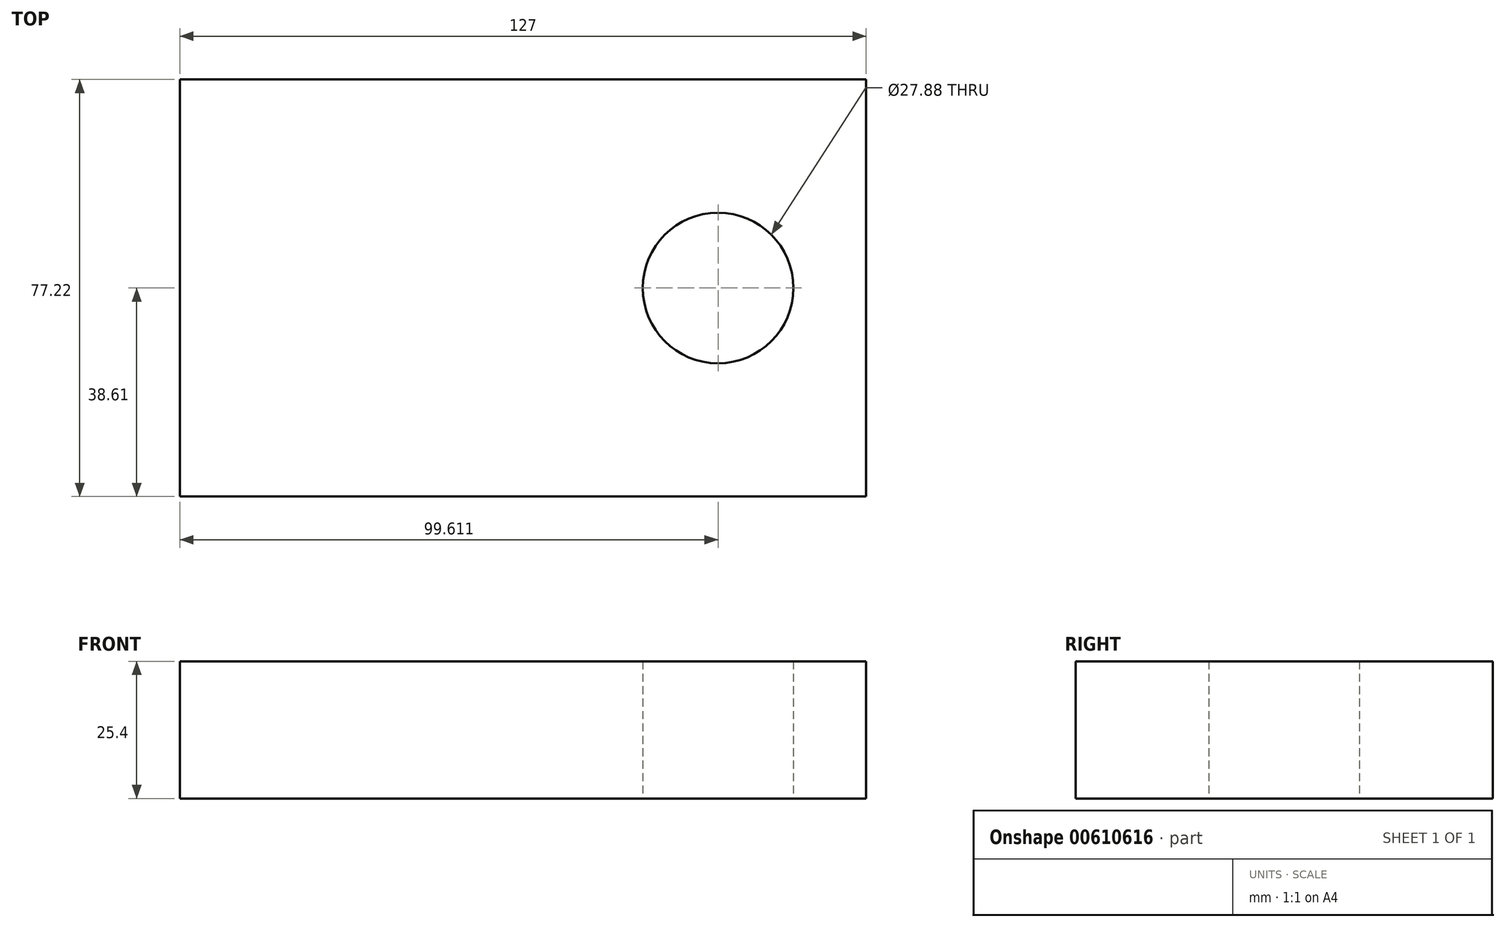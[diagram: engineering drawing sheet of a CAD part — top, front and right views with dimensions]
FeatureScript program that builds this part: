
annotation { "Feature Type Name" : "Feature", "Feature Type Description" : "" }
export const myFeature = defineFeature(function(context is Context, id is Id, definition is map)
    precondition{}
    {
        {
            var Q0;
            Q0=qCreatedBy(makeId("Top.planeOp"),FACE);
            var sketch = newSketch(context, id + "F0", { "sketchPlane" : qUnion([Q0])});
            skLineSegment(sketch, "E0.bottom", {"start": v(63.5, 38.6) * mm, "end": v(-63.5, 38.6) * mm});
            skLineSegment(sketch, "E0.top", {"start": v(63.5, -38.6) * mm, "end": v(-63.5, -38.6) * mm});
            skLineSegment(sketch, "E0.left", {"start": v(63.5, 38.6) * mm, "end": v(63.5, -38.6) * mm});
            skLineSegment(sketch, "E0.right", {"start": v(-63.5, 38.6) * mm, "end": v(-63.5, -38.6) * mm});
            skPoint(sketch, "E0.middle", {"position": v(0, 0) * mm});
            skCircle(sketch, "E1", {"center": v(36.11, 0) * mm, "radius": 13.94 * mm});
            skSolve(sketch);
        }
        {
            var Q0;
            Q0 = qSketchRegion(id + "F0", true);
            extrude(context, id + "F1", {"entities" : qUnion([Q0]), "depth" : 25.4 * mm, "offsetDistance" : 25.4 * mm});
        }
        {
            var Q0;
            Q0 = qSketchRegion(id + "F0", true);
            var Q1;
            Q1 = qConstructionFilter(qBodyType(qCreatedBy(id + "F0" ,EDGE), BodyType.WIRE), ConstructionObject.NO);
            extrude(context, id + "F2", {"entities" : qUnion([Q0]), "bodyType" : ToolBodyType.SURFACE, "surfaceEntities" : qUnion([Q1]), "oppositeDirection" : true, "depth" : 25.4 * mm, "offsetDistance" : 25.4 * mm});
        }
    });
